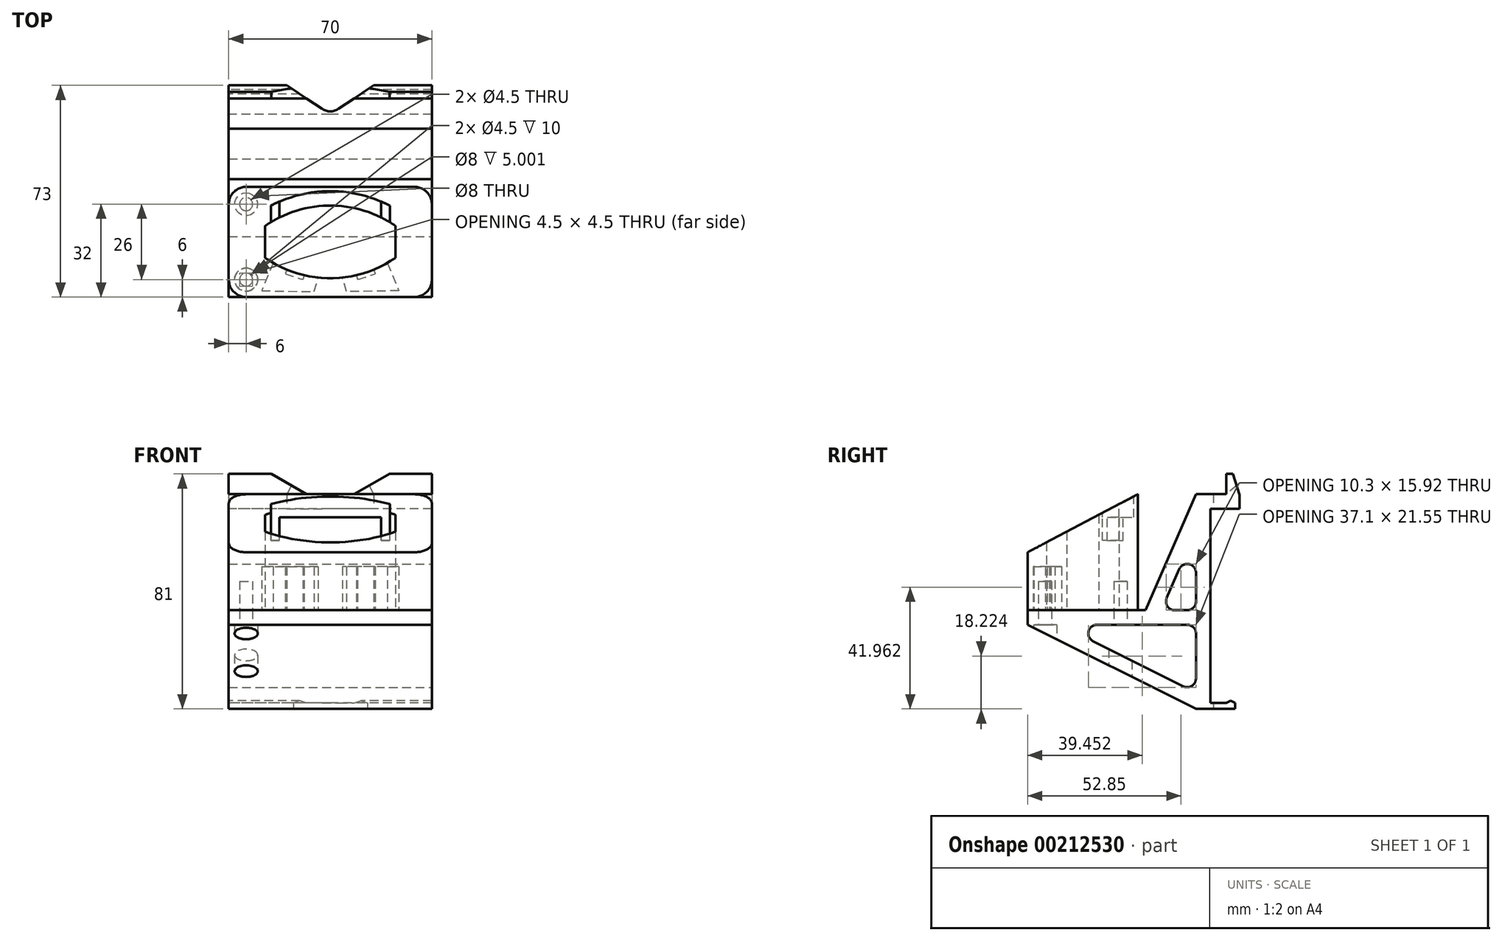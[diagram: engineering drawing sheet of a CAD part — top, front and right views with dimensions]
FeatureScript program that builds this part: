
annotation { "Feature Type Name" : "Feature", "Feature Type Description" : "" }
export const myFeature = defineFeature(function(context is Context, id is Id, definition is map)
    precondition{}
    {
        {
            var Q0;
            Q0=qCreatedBy(makeId("Top.planeOp"),FACE);
            var sketch = newSketch(context, id + "F0", { "sketchPlane" : qUnion([Q0])});
            skLineSegment(sketch, "E0.bottom", {"start": v(35, 19) * mm, "end": v(-35, 19) * mm});
            skLineSegment(sketch, "E0.top", {"start": v(35, -19) * mm, "end": v(-35, -19) * mm});
            skLineSegment(sketch, "E0.left", {"start": v(35, 19) * mm, "end": v(35, -19) * mm});
            skLineSegment(sketch, "E0.right", {"start": v(-35, 19) * mm, "end": v(-35, -19) * mm});
            skPoint(sketch, "E0.middle", {"position": v(0, 0) * mm});
            skSolve(sketch);
        }
        {
            var Q0;
            Q0=makeQuery(id+"F0.imprint","IMPRINT",FACE,{"disambiguationData":[TD([[makeQuery(id+"F0.imprint","IMPRINT",EDGE,{"derivedFrom":sQuery(id+"F0.wireOp",EDGE,"E0.bottom")}),1.0]])]});
            extrude(context, id + "F1", {"entities" : qUnion([Q0]), "depth" : 40 * mm});
        }
        {
            var Q0;
            Q0=makeQuery(id+"F1.opExtrude","CAP_FACE",FACE,{"disambiguationData":[OSD([sQuery(id+"F0.wireOp",EDGE,"E0.bottom"),sQuery(id+"F0.wireOp",EDGE,"E0.top"),sQuery(id+"F0.wireOp",EDGE,"E0.left"),sQuery(id+"F0.wireOp",EDGE,"E0.right")])],"isStart":true});
            var sketch = newSketch(context, id + "F2", { "sketchPlane" : qUnion([Q0])});
            skLineSegment(sketch, "E1.bottom", {"start": v(22.5, -12.5) * mm, "end": v(-22.5, -12.5) * mm, "construction": true});
            skLineSegment(sketch, "E1.top", {"start": v(22.5, 12.5) * mm, "end": v(-22.5, 12.5) * mm, "construction": true});
            skLineSegment(sketch, "E1.left", {"start": v(22.5, -12.5) * mm, "end": v(22.5, 12.5) * mm, "construction": true});
            skLineSegment(sketch, "E1.right", {"start": v(-22.5, -12.5) * mm, "end": v(-22.5, 12.5) * mm, "construction": true});
            skPoint(sketch, "E1.middle", {"position": v(0, 0) * mm});
            skLineSegment(sketch, "E2", {"start": v(-22.5, 0) * mm, "end": v(-22.5, 5.5) * mm, "construction": true});
            skLineSegment(sketch, "E3", {"start": v(-22.5, 5.5) * mm, "end": v(22.5, 5.5) * mm, "construction": true});
            skLineSegment(sketch, "E4", {"start": v(22.5, 5.5) * mm, "end": v(22.5, -5.5) * mm, "construction": true});
            skLineSegment(sketch, "E5", {"start": v(22.5, -5.5) * mm, "end": v(-22.5, -5.5) * mm, "construction": true});
            skArc(sketch, "E6", {"start": v(22.5, 5.5) * mm, "mid": v(0, 12.53) * mm, "end": v(-22.5, 5.5) * mm});
            skLineSegment(sketch, "E7", {"start": v(-22.5, 0) * mm, "end": v(22.5, 0) * mm, "construction": true});
            skArc(sketch, "E8.MirrorCS", {"start": v(22.5, -5.5) * mm, "mid": v(0, -12.53) * mm, "end": v(-22.5, -5.5) * mm});
            skLineSegment(sketch, "E9", {"start": v(-22.5, 5.5) * mm, "end": v(-22.5, -5.5) * mm});
            skLineSegment(sketch, "E10", {"start": v(22.5, 5.5) * mm, "end": v(22.5, -5.5) * mm});
            skSolve(sketch);
        }
        {
            var Q0;
            Q0=makeQuery(id+"F2.imprint","IMPRINT",FACE,{"disambiguationData":[TD([[makeQuery(id+"F2.imprint","IMPRINT",EDGE,{"derivedFrom":sQuery(id+"F2.wireOp",EDGE,"E6")}),1.0]])]});
            extrude(context, id + "F3", {"entities" : qUnion([Q0]), "operationType" : NewBodyOperationType.REMOVE, "endBound" : BoundingType.UP_TO_NEXT, "oppositeDirection" : true, "depth" : 25 * mm});
        }
        {
            var Q0;
            Q0=makeQuery(id+"F1.opExtrude","CAP_FACE",FACE,{"disambiguationData":[OSD([sQuery(id+"F0.wireOp",EDGE,"E0.bottom"),sQuery(id+"F0.wireOp",EDGE,"E0.top"),sQuery(id+"F0.wireOp",EDGE,"E0.left"),sQuery(id+"F0.wireOp",EDGE,"E0.right")])],"isStart":false});
            var sketch = newSketch(context, id + "F4", { "sketchPlane" : qUnion([Q0])});
            skLineSegment(sketch, "E11", {"start": v(0, 0) * mm, "end": v(-20.5, 0) * mm, "construction": true});
            skLineSegment(sketch, "E12", {"start": v(-20.5, 0) * mm, "end": v(-20.5, 38.9) * mm, "construction": true});
            skLineSegment(sketch, "E13", {"start": v(-20.5, 38.9) * mm, "end": v(20.5, 38.9) * mm, "construction": true});
            skLineSegment(sketch, "E14", {"start": v(20.5, 38.9) * mm, "end": v(20.5, 0) * mm, "construction": true});
            skArc(sketch, "E15", {"start": v(20.5, 6.8) * mm, "mid": v(0, 12.53) * mm, "end": v(-20.5, 6.8) * mm});
            skArc(sketch, "E16.0", {"start": v(20.5, 12.53) * mm, "mid": v(0, 17.53) * mm, "end": v(-20.5, 12.53) * mm});
            skLineSegment(sketch, "E17", {"start": v(-20.5, 12.53) * mm, "end": v(-20.5, 6.8) * mm});
            skLineSegment(sketch, "E18", {"start": v(20.5, 12.53) * mm, "end": v(20.5, 6.8) * mm});
            skSolve(sketch);
        }
        {
            var Q0;
            Q0=makeQuery(id+"F4.imprint","IMPRINT",FACE,{"disambiguationData":[TD([[makeQuery(id+"F4.imprint","IMPRINT",EDGE,{"derivedFrom":sQuery(id+"F4.wireOp",EDGE,"E15")}),-1.0]])]});
            extrude(context, id + "F5", {"entities" : qUnion([Q0]), "operationType" : NewBodyOperationType.REMOVE, "oppositeDirection" : true, "depth" : 8 * mm});
        }
        {
            var Q0;
            Q0=makeQuery(id+"F1.opExtrude","CAP_FACE",FACE,{"disambiguationData":[OSD([sQuery(id+"F0.wireOp",EDGE,"E0.bottom"),sQuery(id+"F0.wireOp",EDGE,"E0.top"),sQuery(id+"F0.wireOp",EDGE,"E0.left"),sQuery(id+"F0.wireOp",EDGE,"E0.right")])],"isStart":true});
            var sketch = newSketch(context, id + "F6", { "sketchPlane" : qUnion([Q0])});
            skLineSegment(sketch, "E19", {"start": v(0, 0) * mm, "end": v(-9, 0) * mm, "construction": true});
            skLineSegment(sketch, "E20", {"start": v(-9, 0) * mm, "end": v(-9, 20.88) * mm, "construction": true});
            skLineSegment(sketch, "E21", {"start": v(-9, 20.88) * mm, "end": v(-15, 20.88) * mm, "construction": true});
            skLineSegment(sketch, "E22", {"start": v(-15, 20.88) * mm, "end": v(-15, 0) * mm, "construction": true});
            skArc(sketch, "E23.0", {"start": v(-9.4, 12.94) * mm, "mid": v(-12.48, 12.02) * mm, "end": v(-15.51, 10.98) * mm});
            skLineSegment(sketch, "E24", {"start": v(-15, 9.57) * mm, "end": v(-15.51, 10.98) * mm});
            skLineSegment(sketch, "E25", {"start": v(-9, 11.5) * mm, "end": v(-9.4, 12.94) * mm});
            skLineSegment(sketch, "E26.0", {"start": v(-19.7, 7.87) * mm, "end": v(-20.21, 9.28) * mm, "construction": true});
            skLineSegment(sketch, "E27.0", {"start": v(-4.18, 12.83) * mm, "end": v(-4.58, 14.28) * mm, "construction": true});
            skLineSegment(sketch, "E28", {"start": v(-19.7, 7.27) * mm, "end": v(-23.67, 16.84) * mm});
            skLineSegment(sketch, "E29", {"start": v(-23.67, 16.84) * mm, "end": v(-5.63, 17.14) * mm});
            skLineSegment(sketch, "E30", {"start": v(-5.63, 17.14) * mm, "end": v(-4.18, 12.31) * mm});
            skArc(sketch, "E31", {"start": v(-4.18, 12.31) * mm, "mid": v(-6.6, 11.96) * mm, "end": v(-9, 11.46) * mm});
            skArc(sketch, "E32.trimOffspring", {"start": v(-15, 9.54) * mm, "mid": v(-17.39, 8.48) * mm, "end": v(-19.7, 7.27) * mm});
            skLineSegment(sketch, "E33.MirrorCS", {"start": v(9, 11.5) * mm, "end": v(9.4, 12.94) * mm});
            skLineSegment(sketch, "E34.MirrorCS", {"start": v(4.18, 12.83) * mm, "end": v(4.58, 14.28) * mm, "construction": true});
            skLineSegment(sketch, "E35.MirrorCS", {"start": v(15, 9.57) * mm, "end": v(15.51, 10.98) * mm});
            skLineSegment(sketch, "E36.MirrorCS", {"start": v(19.7, 7.27) * mm, "end": v(23.67, 16.84) * mm});
            skArc(sketch, "E37.MirrorCS", {"start": v(9.4, 12.94) * mm, "mid": v(12.48, 12.02) * mm, "end": v(15.51, 10.98) * mm});
            skLineSegment(sketch, "E38.MirrorCS", {"start": v(23.67, 16.84) * mm, "end": v(5.63, 17.14) * mm});
            skLineSegment(sketch, "E39.MirrorCS", {"start": v(5.63, 17.14) * mm, "end": v(4.18, 12.31) * mm});
            skArc(sketch, "E40.MirrorCS", {"start": v(4.18, 12.31) * mm, "mid": v(6.6, 11.96) * mm, "end": v(9, 11.46) * mm});
            skArc(sketch, "E41.MirrorCS", {"start": v(15, 9.54) * mm, "mid": v(17.39, 8.48) * mm, "end": v(19.7, 7.27) * mm});
            skLineSegment(sketch, "E42.MirrorCS", {"start": v(19.7, 7.87) * mm, "end": v(20.21, 9.28) * mm, "construction": true});
            skSolve(sketch);
        }
        {
            var Q0;
            Q0=makeQuery(id+"F6.imprint","IMPRINT",FACE,{"disambiguationData":[TD([[makeQuery(id+"F6.imprint","IMPRINT",EDGE,{"derivedFrom":sQuery(id+"F6.wireOp",EDGE,"E23.0")}),-1.0]])]});
            var Q1;
            {var subQ2=sQuery(id+"F6.wireOp",EDGE,"E33.MirrorCS");Q1=makeQuery(id+"F6.imprint","IMPRINT",FACE,{"disambiguationData":[TD([[makeQuery(id+"F6.imprint","IMPRINT",EDGE,{"derivedFrom":subQ2}),1.0]])]});}
            extrude(context, id + "F7", {"entities" : qUnion([Q0, Q1]), "operationType" : NewBodyOperationType.REMOVE, "oppositeDirection" : true, "depth" : 15 * mm});
        }
        {
            var Q0;
            Q0=makeQuery(id+"F1.opExtrude","SWEPT_FACE",FACE,{"disambiguationData":[OSD([sQuery(id+"F0.wireOp",EDGE,"E0.left")])]});
            var sketch = newSketch(context, id + "F8", { "sketchPlane" : qUnion([Q0])});
            skLineSegment(sketch, "E43", {"start": v(19, 40) * mm, "end": v(-19, 40) * mm});
            skLineSegment(sketch, "E44", {"start": v(-19, 40) * mm, "end": v(-19, 20) * mm});
            skLineSegment(sketch, "E45", {"start": v(-19, 20) * mm, "end": v(19, 40) * mm});
            skSolve(sketch);
        }
        {
            var Q0;
            Q0=makeQuery(id+"F8.imprint","IMPRINT",FACE,{"disambiguationData":[TD([[makeQuery(id+"F8.imprint","IMPRINT",EDGE,{"derivedFrom":sQuery(id+"F8.wireOp",EDGE,"E43")}),1.0]])]});
            extrude(context, id + "F9", {"entities" : qUnion([Q0]), "operationType" : NewBodyOperationType.REMOVE, "endBound" : BoundingType.THROUGH_ALL, "oppositeDirection" : true, "depth" : 25 * mm});
        }
        {
            var Q0;
            Q0=qCreatedBy(makeId("Right.planeOp"),FACE);
            var sketch = newSketch(context, id + "F10", { "sketchPlane" : qUnion([Q0])});
            skLineSegment(sketch, "E46", {"start": v(0, 0) * mm, "end": v(21.67, 0) * mm});
            skLineSegment(sketch, "E47", {"start": v(39, 0) * mm, "end": v(39, 27.42) * mm});
            skLineSegment(sketch, "E48", {"start": v(39, 40) * mm, "end": v(49.5, 40) * mm});
            skLineSegment(sketch, "E49", {"start": v(49.5, 40) * mm, "end": v(49.5, 47) * mm});
            skLineSegment(sketch, "E50", {"start": v(49.5, 47) * mm, "end": v(51.75, 47) * mm});
            skLineSegment(sketch, "E51", {"start": v(54, 39.87) * mm, "end": v(54, 35) * mm});
            skLineSegment(sketch, "E52", {"start": v(54, 35) * mm, "end": v(44, 35) * mm});
            skLineSegment(sketch, "E53", {"start": v(44, 35) * mm, "end": v(44, -32) * mm});
            skLineSegment(sketch, "E54", {"start": v(44, -32) * mm, "end": v(49.5, -32) * mm});
            skLineSegment(sketch, "E55", {"start": v(52.5, -32) * mm, "end": v(52.5, -34) * mm});
            skLineSegment(sketch, "E56", {"start": v(52.5, -34) * mm, "end": v(39, -34) * mm});
            skLineSegment(sketch, "E57", {"start": v(39, -5) * mm, "end": v(39, -28.4) * mm});
            skLineSegment(sketch, "E58", {"start": v(51.75, 47) * mm, "end": v(54, 39.87) * mm});
            skPoint(sketch, "E59.orphan", {"position": v(54, 47) * mm});
            skLineSegment(sketch, "E60", {"start": v(49.5, -32) * mm, "end": v(51, -31.25) * mm});
            skLineSegment(sketch, "E61", {"start": v(51, -31.25) * mm, "end": v(52.5, -32) * mm});
            skLineSegment(sketch, "E62", {"start": v(0, 0) * mm, "end": v(-19, 0) * mm});
            skLineSegment(sketch, "E63", {"start": v(-19, 0) * mm, "end": v(-19, -5) * mm});
            skLineSegment(sketch, "E64", {"start": v(-7.82, -5) * mm, "end": v(39, -5) * mm});
            skLineSegment(sketch, "E65", {"start": v(39, 40) * mm, "end": v(21.67, 0) * mm});
            skLineSegment(sketch, "E66.0", {"start": v(39, 27.42) * mm, "end": v(27.12, 0) * mm});
            skLineSegment(sketch, "E67.trimOffspring", {"start": v(27.12, 0) * mm, "end": v(39, 0) * mm});
            skLineSegment(sketch, "E68", {"start": v(39, -34) * mm, "end": v(-19, -5) * mm});
            skLineSegment(sketch, "E69.0", {"start": v(39, -28.4) * mm, "end": v(-7.82, -5) * mm});
            skSolve(sketch);
        }
        {
            var Q0;
            Q0=makeQuery(id+"F10.imprint","IMPRINT",FACE,{"disambiguationData":[TD([[makeQuery(id+"F10.imprint","IMPRINT",EDGE,{"derivedFrom":sQuery(id+"F10.wireOp",EDGE,"E46")}),-1.0]])]});
            extrude(context, id + "F11", {"entities" : qUnion([Q0]), "endBound" : BoundingType.SYMMETRIC, "depth" : 70 * mm});
        }
        {
            var Q0;
            Q0=makeQuery(id+"F11.opExtrude","SWEPT_FACE",FACE,{"disambiguationData":[OSD([sQuery(id+"F10.wireOp",EDGE,"E56")])]});
            var sketch = newSketch(context, id + "F12", { "sketchPlane" : qUnion([Q0])});
            skLineSegment(sketch, "E70", {"start": v(-35, -39) * mm, "end": v(-29, -39) * mm, "construction": true});
            skLineSegment(sketch, "E71", {"start": v(-29, -39) * mm, "end": v(-29, -13) * mm, "construction": true});
            skLineSegment(sketch, "E72", {"start": v(-29, -13) * mm, "end": v(-29, 13) * mm, "construction": true});
            skCircle(sketch, "E73", {"center": v(-29, 13) * mm, "radius": 2.25 * mm});
            skCircle(sketch, "E74", {"center": v(-29, -13) * mm, "radius": 2.25 * mm});
            skCircle(sketch, "E75.MirrorC", {"center": v(29, 13) * mm, "radius": 2.25 * mm});
            skCircle(sketch, "E76.MirrorC", {"center": v(29, -13) * mm, "radius": 2.25 * mm});
            skSolve(sketch);
        }
        {
            var Q0;
            Q0=makeQuery(id+"F12.imprint","IMPRINT",FACE,{"disambiguationData":[TD([[makeQuery(id+"F12.imprint","IMPRINT",EDGE,{"derivedFrom":sQuery(id+"F12.wireOp",EDGE,"E73")}),1.0]])]});
            var Q1;
            Q1=makeQuery(id+"F12.imprint","IMPRINT",FACE,{"disambiguationData":[TD([[makeQuery(id+"F12.imprint","IMPRINT",EDGE,{"derivedFrom":sQuery(id+"F12.wireOp",EDGE,"E75.MirrorC")}),-1.0]])]});
            var Q2;
            Q2=makeQuery(id+"F12.imprint","IMPRINT",FACE,{"disambiguationData":[TD([[makeQuery(id+"F12.imprint","IMPRINT",EDGE,{"derivedFrom":sQuery(id+"F12.wireOp",EDGE,"E74")}),1.0]])]});
            var Q3;
            Q3=makeQuery(id+"F12.imprint","IMPRINT",FACE,{"disambiguationData":[TD([[makeQuery(id+"F12.imprint","IMPRINT",EDGE,{"derivedFrom":sQuery(id+"F12.wireOp",EDGE,"E76.MirrorC")}),-1.0]])]});
            extrude(context, id + "F13", {"entities" : qUnion([Q0, Q1, Q2, Q3]), "operationType" : NewBodyOperationType.REMOVE, "oppositeDirection" : true, "depth" : 44 * mm});
        }
        {
            var Q0;
            Q0=makeQuery(id+"F11.opExtrude","SWEPT_FACE",FACE,{"disambiguationData":[OSD([sQuery(id+"F10.wireOp",EDGE,"E56")])]});
            var sketch = newSketch(context, id + "F14", { "sketchPlane" : qUnion([Q0])});
            skLineSegment(sketch, "E77", {"start": v(-35, -39) * mm, "end": v(-29, -39) * mm, "construction": true});
            skLineSegment(sketch, "E78", {"start": v(-29, -39) * mm, "end": v(-29, -13) * mm, "construction": true});
            skLineSegment(sketch, "E79", {"start": v(-29, -13) * mm, "end": v(-29, 13) * mm, "construction": true});
            skCircle(sketch, "E80", {"center": v(-29, -13) * mm, "radius": 4 * mm});
            skCircle(sketch, "E81", {"center": v(-29, 13) * mm, "radius": 4 * mm});
            skLineSegment(sketch, "E82", {"start": v(0, -39) * mm, "end": v(0, -12) * mm, "construction": true});
            skPoint(sketch, "E82.endSnap0", {"position": v(0, -39) * mm});
            skCircle(sketch, "E83.MirrorC", {"center": v(29, 13) * mm, "radius": 4 * mm});
            skCircle(sketch, "E84.MirrorC", {"center": v(29, -13) * mm, "radius": 4 * mm});
            skSolve(sketch);
        }
        {
            var Q0;
            Q0=makeQuery(id+"F14.imprint","IMPRINT",FACE,{"disambiguationData":[TD([[makeQuery(id+"F14.imprint","IMPRINT",EDGE,{"derivedFrom":sQuery(id+"F14.wireOp",EDGE,"E81")}),1.0]])]});
            var Q1;
            Q1=makeQuery(id+"F14.imprint","IMPRINT",FACE,{"disambiguationData":[TD([[makeQuery(id+"F14.imprint","IMPRINT",EDGE,{"derivedFrom":sQuery(id+"F14.wireOp",EDGE,"E83.MirrorC")}),-1.0]])]});
            var Q2;
            Q2=makeQuery(id+"F14.imprint","IMPRINT",FACE,{"disambiguationData":[TD([[makeQuery(id+"F14.imprint","IMPRINT",EDGE,{"derivedFrom":sQuery(id+"F14.wireOp",EDGE,"E80")}),1.0]])]});
            var Q3;
            Q3=makeQuery(id+"F14.imprint","IMPRINT",FACE,{"disambiguationData":[TD([[makeQuery(id+"F14.imprint","IMPRINT",EDGE,{"derivedFrom":sQuery(id+"F14.wireOp",EDGE,"E84.MirrorC")}),-1.0]])]});
            extrude(context, id + "F15", {"entities" : qUnion([Q0, Q1, Q2, Q3]), "operationType" : NewBodyOperationType.REMOVE, "oppositeDirection" : true, "depth" : 29 * mm});
        }
        {
            var Q0;
            Q0=makeQuery(id+"F1.opExtrude","SWEPT_EDGE",EDGE,{"disambiguationData":[OSD([sQuery(id+"F0.wireOp",EDGE,"E0.bottom"),sQuery(id+"F0.wireOp",EDGE,"E0.left")])]});
            var Q1;
            Q1=makeQuery(id+"F1.opExtrude","SWEPT_EDGE",EDGE,{"disambiguationData":[OSD([sQuery(id+"F0.wireOp",EDGE,"E0.top"),sQuery(id+"F0.wireOp",EDGE,"E0.left")])]});
            var Q2;
            Q2=makeQuery(id+"F1.opExtrude","SWEPT_EDGE",EDGE,{"disambiguationData":[OSD([sQuery(id+"F0.wireOp",EDGE,"E0.top"),sQuery(id+"F0.wireOp",EDGE,"E0.right")])]});
            var Q3;
            Q3=makeQuery(id+"F1.opExtrude","SWEPT_EDGE",EDGE,{"disambiguationData":[OSD([sQuery(id+"F0.wireOp",EDGE,"E0.bottom"),sQuery(id+"F0.wireOp",EDGE,"E0.right")])]});
            fillet(context, id + "F16", {"entities" : qUnion([Q0, Q1, Q2, Q3]), "radius" : 6 * mm, "tangentPropagation" : true, "allowEdgeOverflow" : false});
        }
        {
            var Q0;
            Q0=makeQuery(id+"F11.opExtrude","SWEPT_EDGE",EDGE,{"disambiguationData":[OSD([sQuery(id+"F10.wireOp",EDGE,"E47"),sQuery(id+"F10.wireOp",EDGE,"E66.0")])]});
            var Q1;
            Q1=makeQuery(id+"F11.opExtrude","SWEPT_EDGE",EDGE,{"disambiguationData":[OSD([sQuery(id+"F10.wireOp",EDGE,"E57"),sQuery(id+"F10.wireOp",EDGE,"E64")])]});
            var Q2;
            Q2=makeQuery(id+"F11.opExtrude","SWEPT_EDGE",EDGE,{"disambiguationData":[OSD([sQuery(id+"F10.wireOp",EDGE,"E66.0"),sQuery(id+"F10.wireOp",EDGE,"E67.trimOffspring")])]});
            var Q3;
            Q3=makeQuery(id+"F11.opExtrude","SWEPT_EDGE",EDGE,{"disambiguationData":[OSD([sQuery(id+"F10.wireOp",EDGE,"E47"),sQuery(id+"F10.wireOp",EDGE,"E67.trimOffspring")])]});
            var Q4;
            Q4=makeQuery(id+"F11.opExtrude","SWEPT_EDGE",EDGE,{"disambiguationData":[OSD([sQuery(id+"F10.wireOp",EDGE,"E57"),sQuery(id+"F10.wireOp",EDGE,"E69.0")])]});
            var Q5;
            Q5=makeQuery(id+"F11.opExtrude","SWEPT_EDGE",EDGE,{"disambiguationData":[OSD([sQuery(id+"F10.wireOp",EDGE,"E64"),sQuery(id+"F10.wireOp",EDGE,"E69.0")])]});
            fillet(context, id + "F17", {"entities" : qUnion([Q0, Q1, Q2, Q3, Q4, Q5]), "radius" : 3 * mm, "tangentPropagation" : true, "allowEdgeOverflow" : false});
        }
        {
            var Q0;
            Q0=makeQuery(id+"F11.opExtrude","SWEPT_FACE",FACE,{"disambiguationData":[OSD([sQuery(id+"F10.wireOp",EDGE,"E52")])]});
            var sketch = newSketch(context, id + "F18", { "sketchPlane" : qUnion([Q0])});
            skLineSegment(sketch, "E85", {"start": v(-35, -54) * mm, "end": v(-15, -54) * mm, "construction": true});
            skLineSegment(sketch, "E86", {"start": v(-15, -54) * mm, "end": v(-15, -44) * mm, "construction": true});
            skLineSegment(sketch, "E87", {"start": v(-15, -44) * mm, "end": v(0, -44) * mm, "construction": true});
            skLineSegment(sketch, "E88", {"start": v(-15, -54) * mm, "end": v(0, -44) * mm});
            skLineSegment(sketch, "E89.MirrorCS", {"start": v(15, -54) * mm, "end": v(0, -44) * mm});
            skLineSegment(sketch, "E90", {"start": v(-15, -54) * mm, "end": v(15, -54) * mm});
            skSolve(sketch);
        }
        {
            var Q0;
            Q0=makeQuery(id+"F18.imprint","IMPRINT",FACE,{"disambiguationData":[TD([[makeQuery(id+"F18.imprint","IMPRINT",EDGE,{"derivedFrom":sQuery(id+"F18.wireOp",EDGE,"E88")}),-1.0]])]});
            extrude(context, id + "F19", {"entities" : qUnion([Q0]), "operationType" : NewBodyOperationType.REMOVE, "endBound" : BoundingType.SYMMETRIC, "oppositeDirection" : true, "depth" : 200 * mm});
        }
        {
            var Q0;
            {var subQ0=sQuery(id+"F18.wireOp",EDGE,"E88");var subQ1=sQuery(id+"F10.wireOp",EDGE,"E53");var subQ2=sQuery(id+"F18.wireOp",EDGE,"E89.MirrorCS");Q0=makeQuery(id+"F19.boolean.opBoolean","COPY",EDGE,{"disambiguationData":[TD([makeQuery(id+"F11.opExtrude","SWEPT_FACE",FACE,{"disambiguationData":[OSD([sQuery(id+"F10.wireOp",EDGE,"E54")])]})])],"derivedFrom":makeQuery(id+"F19.opExtrude","SWEPT_EDGE",EDGE,{"disambiguationData":[OSD([sQuery(id+"F10.wireOp",EDGE,"E52"),subQ1,subQ0,subQ2])]})});}
            var Q1;
            {var subQ0=sQuery(id+"F18.wireOp",EDGE,"E88");var subQ1=sQuery(id+"F10.wireOp",EDGE,"E52");var subQ2=sQuery(id+"F10.wireOp",EDGE,"E53");var subQ3=sQuery(id+"F18.wireOp",EDGE,"E89.MirrorCS");Q1=makeQuery(id+"F19.boolean.opBoolean","COPY",EDGE,{"disambiguationData":[TD([makeQuery(id+"F11.opExtrude","SWEPT_FACE",FACE,{"disambiguationData":[OSD([sQuery(id+"F10.wireOp",EDGE,"E48")])]})])],"derivedFrom":makeQuery(id+"F19.opExtrude","SWEPT_EDGE",EDGE,{"disambiguationData":[OSD([subQ1,subQ2,subQ0,subQ3])]})});}
            fillet(context, id + "F20", {"entities" : qUnion([Q0, Q1]), "radius" : 5 * mm, "tangentPropagation" : true, "allowEdgeOverflow" : false});
        }
        {
            var Q0;
            Q0=makeQuery(id+"F5.boolean.opBoolean","COPY",FACE,{"derivedFrom":makeQuery(id+"F5.opExtrude","CAP_FACE",FACE,{"disambiguationData":[OSD([sQuery(id+"F4.wireOp",EDGE,"E15"),sQuery(id+"F4.wireOp",EDGE,"E16.0"),sQuery(id+"F4.wireOp",EDGE,"E17"),sQuery(id+"F4.wireOp",EDGE,"E18")])],"isStart":false})});
            var sketch = newSketch(context, id + "F21", { "sketchPlane" : qUnion([Q0])});
            skLineSegment(sketch, "E91", {"start": v(-20.5, 6.8) * mm, "end": v(-20.5, 12.53) * mm});
            skLineSegment(sketch, "E92", {"start": v(-20.5, 6.8) * mm, "end": v(-17.5, 6.8) * mm, "construction": true});
            skLineSegment(sketch, "E93", {"start": v(-17.5, 6.8) * mm, "end": v(-17.5, 16.42) * mm, "construction": true});
            skLineSegment(sketch, "E94", {"start": v(-17.5, 8.45) * mm, "end": v(-17.5, 13.95) * mm});
            skArc(sketch, "E95", {"start": v(-17.5, 13.95) * mm, "mid": v(-19.01, 13.26) * mm, "end": v(-20.5, 12.53) * mm});
            skLineSegment(sketch, "E96", {"start": v(-17.5, 8.45) * mm, "end": v(-17.5, 6.8) * mm});
            skLineSegment(sketch, "E97", {"start": v(-17.5, 6.8) * mm, "end": v(-20.5, 6.8) * mm});
            skLineSegment(sketch, "E98", {"start": v(0, 12.53) * mm, "end": v(0, 6.49) * mm, "construction": true});
            skPoint(sketch, "E98.endSnap0", {"position": v(0, 12.53) * mm});
            skLineSegment(sketch, "E99.MirrorCS", {"start": v(17.5, 6.8) * mm, "end": v(20.5, 6.8) * mm});
            skLineSegment(sketch, "E100.MirrorCS", {"start": v(20.5, 6.8) * mm, "end": v(17.5, 6.8) * mm, "construction": true});
            skLineSegment(sketch, "E101.MirrorCS", {"start": v(20.5, 6.8) * mm, "end": v(20.5, 12.53) * mm});
            skLineSegment(sketch, "E102.MirrorCS", {"start": v(17.5, 8.45) * mm, "end": v(17.5, 13.95) * mm});
            skLineSegment(sketch, "E103.MirrorCS", {"start": v(17.5, 8.45) * mm, "end": v(17.5, 6.8) * mm});
            skArc(sketch, "E104.MirrorCS", {"start": v(17.5, 13.95) * mm, "mid": v(19.01, 13.26) * mm, "end": v(20.5, 12.53) * mm});
            skSolve(sketch);
        }
        {
            var Q0;
            {var subQ0=sQuery(id+"F21.wireOp",EDGE,"E91");Q0=makeQuery(id+"F21.imprint","IMPRINT",FACE,{"disambiguationData":[TD([[makeQuery(id+"F21.imprint","IMPRINT",EDGE,{"derivedFrom":subQ0}),1.0]])]});}
            var Q1;
            {var subQ0=sQuery(id+"F21.wireOp",EDGE,"E101.MirrorCS");Q1=makeQuery(id+"F21.imprint","IMPRINT",FACE,{"disambiguationData":[TD([[makeQuery(id+"F21.imprint","IMPRINT",EDGE,{"derivedFrom":subQ0}),-1.0]])]});}
            extrude(context, id + "F22", {"entities" : qUnion([Q0, Q1]), "operationType" : NewBodyOperationType.REMOVE, "oppositeDirection" : true, "depth" : 8 * mm});
        }
        {
            var Q0;
            {var subQ1=sQuery(id+"F10.wireOp",EDGE,"E49");Q0=makeQuery(id+"F19.boolean.opBoolean","SPLIT",FACE,{"disambiguationData":[TD([makeQuery(id+"F19.opExtrude","SWEPT_FACE",FACE,{"disambiguationData":[OSD([sQuery(id+"F18.wireOp",EDGE,"E88")])]})])],"derivedFrom":makeQuery(id+"F11.opExtrude","SWEPT_FACE",FACE,{"disambiguationData":[OSD([subQ1])]})});}
            var sketch = newSketch(context, id + "F23", { "sketchPlane" : qUnion([Q0])});
            skLineSegment(sketch, "E105", {"start": v(0, 0) * mm, "end": v(0, 55.52) * mm, "construction": true});
            skLineSegment(sketch, "E106", {"start": v(-8.25, 40) * mm, "end": v(-8.25, 47) * mm});
            skLineSegment(sketch, "E107", {"start": v(-8.25, 40) * mm, "end": v(-20.37, 47) * mm});
            skLineSegment(sketch, "E108", {"start": v(-20.37, 47) * mm, "end": v(-8.25, 47) * mm});
            skLineSegment(sketch, "E109.MirrorCS", {"start": v(8.25, 40) * mm, "end": v(20.37, 47) * mm});
            skLineSegment(sketch, "E110.MirrorCS", {"start": v(20.37, 47) * mm, "end": v(8.25, 47) * mm});
            skLineSegment(sketch, "E111.MirrorCS", {"start": v(8.25, 40) * mm, "end": v(8.25, 47) * mm});
            skSolve(sketch);
        }
        {
            var Q0;
            Q0=makeQuery(id+"F23.imprint","IMPRINT",FACE,{"disambiguationData":[TD([[makeQuery(id+"F23.imprint","IMPRINT",EDGE,{"derivedFrom":sQuery(id+"F23.wireOp",EDGE,"E106")}),1.0]])]});
            var Q1;
            Q1=makeQuery(id+"F23.imprint","IMPRINT",FACE,{"disambiguationData":[TD([[makeQuery(id+"F23.imprint","IMPRINT",EDGE,{"derivedFrom":sQuery(id+"F23.wireOp",EDGE,"E109.MirrorCS")}),1.0]])]});
            extrude(context, id + "F24", {"entities" : qUnion([Q0, Q1]), "operationType" : NewBodyOperationType.REMOVE, "endBound" : BoundingType.UP_TO_NEXT, "oppositeDirection" : true, "depth" : 25 * mm});
        }
    });
